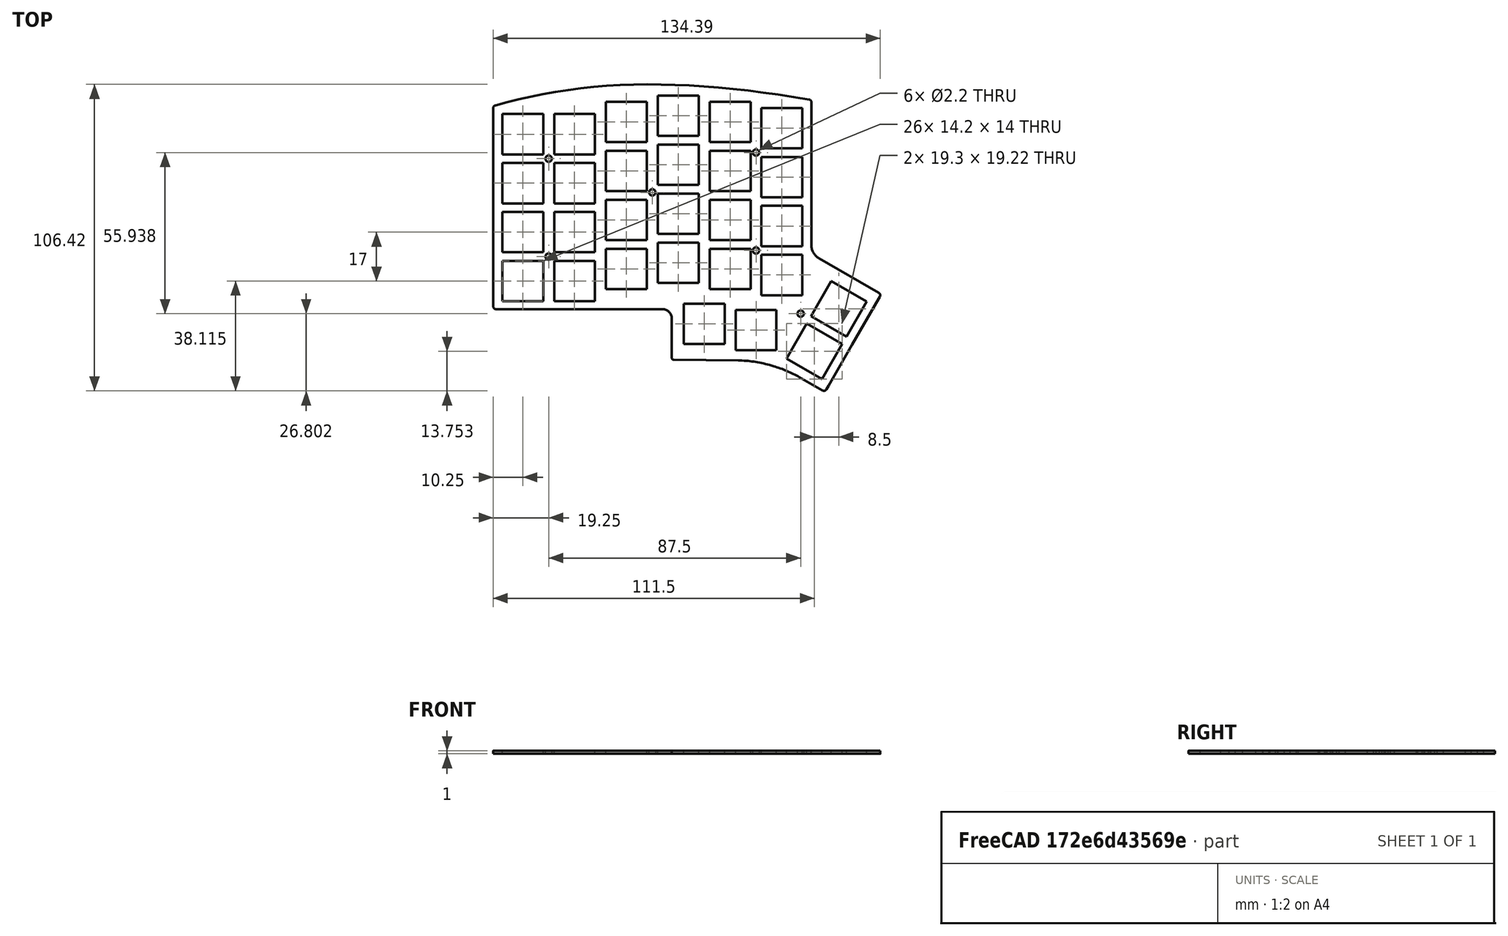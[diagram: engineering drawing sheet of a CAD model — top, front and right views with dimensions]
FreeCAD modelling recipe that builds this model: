
FCSTD DOCUMENT  (FreeCAD 0.19R)
Label: iris_plate_support_extruded
License: All rights reserved
LicenseURL: http://en.wikipedia.org/wiki/All_rights_reserved
objects: Part::Feature×35, Part::Extrusion×35, App::LinkGroup×1, Part::FeaturePython×1
note: 71 computed .brp shape members not serialized (recipe doc carries the construction recipe); baked Part::Feature solids carry a one-line shape summary decoded from their .brp

FEATURE [Part::Feature] Face
  shape: bbox 2.2 x 2.2 x 2e-07 mm, 1 faces, 0 solids (baked)
FEATURE [Part::Feature] Face001 .. Face005  x5 (patterned run collapsed; names and placements below)
  shape: bbox 2.2 x 2.2 x 2e-07 mm, 1 faces, 0 solids (baked)
FEATURE [Part::Feature] Face006 .. Face021  x16 (patterned run collapsed; names and placements below)
  shape: bbox 14.2 x 14 x 2e-07 mm, 1 faces, 0 solids (baked)
FEATURE [Part::Feature] Face022
  shape: bbox 19.3 x 19.22 x 2e-07 mm, 1 faces, 0 solids (baked)
FEATURE [Part::Feature] Face023 .. Face030  x8 (patterned run collapsed; names and placements below)
  shape: bbox 14.2 x 14 x 2e-07 mm, 1 faces, 0 solids (baked)
FEATURE [Part::Feature] Face031
  shape: bbox 19.3 x 19.22 x 2e-07 mm, 1 faces, 0 solids (baked)
FEATURE [Part::Feature] Face032
  shape: bbox 14.2 x 14 x 2e-07 mm, 1 faces, 0 solids (baked)
FEATURE [Part::Feature] Face033
  shape: bbox 14.2 x 14 x 2e-07 mm, 1 faces, 0 solids (baked)
FEATURE [Part::Feature] Face034
  shape: bbox 134.4 x 106.7 x 2e-07 mm, 1 faces, 0 solids (baked)
FEATURE [Part::Extrusion] Extrude
  Base = -> Face034
  Dir = (0,0,1)
  DirMode = 0
  FaceMakerClass = Part::FaceMakerBullseye
  LengthFwd = 1
  LengthRev = 0
  Solid = true
  Symmetric = false
FEATURE [Part::Extrusion] Extrude001
  Base = -> Face033
  Dir = (0,0,1)
  DirMode = 0
  FaceMakerClass = Part::FaceMakerBullseye
  LengthFwd = 1
  LengthRev = 0
  Solid = true
  Symmetric = false
FEATURE [Part::Extrusion] Extrude002
  Base = -> Face032
  Dir = (0,0,1)
  DirMode = 0
  FaceMakerClass = Part::FaceMakerBullseye
  LengthFwd = 1
  LengthRev = 0
  Solid = true
  Symmetric = false
FEATURE [Part::Extrusion] Extrude003
  Base = -> Face031
  Dir = (0,0,1)
  DirMode = 0
  FaceMakerClass = Part::FaceMakerBullseye
  LengthFwd = 1
  LengthRev = 0
  Solid = true
  Symmetric = false
FEATURE [Part::Extrusion] Extrude004
  Base = -> Face030
  Dir = (0,0,1)
  DirMode = 0
  FaceMakerClass = Part::FaceMakerBullseye
  LengthFwd = 1
  LengthRev = 0
  Solid = true
  Symmetric = false
FEATURE [Part::Extrusion] Extrude005
  Base = -> Face029
  Dir = (0,0,1)
  DirMode = 0
  FaceMakerClass = Part::FaceMakerBullseye
  LengthFwd = 1
  LengthRev = 0
  Solid = true
  Symmetric = false
FEATURE [Part::Extrusion] Extrude006
  Base = -> Face028
  Dir = (0,0,1)
  DirMode = 0
  FaceMakerClass = Part::FaceMakerBullseye
  LengthFwd = 1
  LengthRev = 0
  Solid = true
  Symmetric = false
FEATURE [Part::Extrusion] Extrude007
  Base = -> Face027
  Dir = (0,0,1)
  DirMode = 0
  FaceMakerClass = Part::FaceMakerBullseye
  LengthFwd = 1
  LengthRev = 0
  Solid = true
  Symmetric = false
FEATURE [Part::Extrusion] Extrude008
  Base = -> Face026
  Dir = (0,0,1)
  DirMode = 0
  FaceMakerClass = Part::FaceMakerBullseye
  LengthFwd = 1
  LengthRev = 0
  Solid = true
  Symmetric = false
FEATURE [Part::Extrusion] Extrude009
  Base = -> Face025
  Dir = (0,0,1)
  DirMode = 0
  FaceMakerClass = Part::FaceMakerBullseye
  LengthFwd = 1
  LengthRev = 0
  Solid = true
  Symmetric = false
FEATURE [Part::Extrusion] Extrude010
  Base = -> Face024
  Dir = (0,0,1)
  DirMode = 0
  FaceMakerClass = Part::FaceMakerBullseye
  LengthFwd = 1
  LengthRev = 0
  Solid = true
  Symmetric = false
FEATURE [Part::Extrusion] Extrude011
  Base = -> Face023
  Dir = (0,0,1)
  DirMode = 0
  FaceMakerClass = Part::FaceMakerBullseye
  LengthFwd = 1
  LengthRev = 0
  Solid = true
  Symmetric = false
FEATURE [Part::Extrusion] Extrude012
  Base = -> Face022
  Dir = (0,0,1)
  DirMode = 0
  FaceMakerClass = Part::FaceMakerBullseye
  LengthFwd = 1
  LengthRev = 0
  Solid = true
  Symmetric = false
FEATURE [Part::Extrusion] Extrude013
  Base = -> Face021
  Dir = (0,0,1)
  DirMode = 0
  FaceMakerClass = Part::FaceMakerBullseye
  LengthFwd = 1
  LengthRev = 0
  Solid = true
  Symmetric = false
FEATURE [Part::Extrusion] Extrude014
  Base = -> Face020
  Dir = (0,0,1)
  DirMode = 0
  FaceMakerClass = Part::FaceMakerBullseye
  LengthFwd = 1
  LengthRev = 0
  Solid = true
  Symmetric = false
FEATURE [Part::Extrusion] Extrude015
  Base = -> Face019
  Dir = (0,0,1)
  DirMode = 0
  FaceMakerClass = Part::FaceMakerBullseye
  LengthFwd = 1
  LengthRev = 0
  Solid = true
  Symmetric = false
FEATURE [Part::Extrusion] Extrude016
  Base = -> Face018
  Dir = (0,0,1)
  DirMode = 0
  FaceMakerClass = Part::FaceMakerBullseye
  LengthFwd = 1
  LengthRev = 0
  Solid = true
  Symmetric = false
FEATURE [Part::Extrusion] Extrude017
  Base = -> Face017
  Dir = (0,0,1)
  DirMode = 0
  FaceMakerClass = Part::FaceMakerBullseye
  LengthFwd = 1
  LengthRev = 0
  Solid = true
  Symmetric = false
FEATURE [Part::Extrusion] Extrude018
  Base = -> Face016
  Dir = (0,0,1)
  DirMode = 0
  FaceMakerClass = Part::FaceMakerBullseye
  LengthFwd = 1
  LengthRev = 0
  Solid = true
  Symmetric = false
FEATURE [Part::Extrusion] Extrude019
  Base = -> Face015
  Dir = (0,0,1)
  DirMode = 0
  FaceMakerClass = Part::FaceMakerBullseye
  LengthFwd = 1
  LengthRev = 0
  Solid = true
  Symmetric = false
FEATURE [Part::Extrusion] Extrude020
  Base = -> Face014
  Dir = (0,0,1)
  DirMode = 0
  FaceMakerClass = Part::FaceMakerBullseye
  LengthFwd = 1
  LengthRev = 0
  Solid = true
  Symmetric = false
FEATURE [Part::Extrusion] Extrude021
  Base = -> Face013
  Dir = (0,0,1)
  DirMode = 0
  FaceMakerClass = Part::FaceMakerBullseye
  LengthFwd = 1
  LengthRev = 0
  Solid = true
  Symmetric = false
FEATURE [Part::Extrusion] Extrude022
  Base = -> Face012
  Dir = (0,0,1)
  DirMode = 0
  FaceMakerClass = Part::FaceMakerBullseye
  LengthFwd = 1
  LengthRev = 0
  Solid = true
  Symmetric = false
FEATURE [Part::Extrusion] Extrude023
  Base = -> Face011
  Dir = (0,0,1)
  DirMode = 0
  FaceMakerClass = Part::FaceMakerBullseye
  LengthFwd = 1
  LengthRev = 0
  Solid = true
  Symmetric = false
FEATURE [Part::Extrusion] Extrude024
  Base = -> Face010
  Dir = (0,0,1)
  DirMode = 0
  FaceMakerClass = Part::FaceMakerBullseye
  LengthFwd = 1
  LengthRev = 0
  Solid = true
  Symmetric = false
FEATURE [Part::Extrusion] Extrude025
  Base = -> Face009
  Dir = (0,0,1)
  DirMode = 0
  FaceMakerClass = Part::FaceMakerBullseye
  LengthFwd = 1
  LengthRev = 0
  Solid = true
  Symmetric = false
FEATURE [Part::Extrusion] Extrude026
  Base = -> Face008
  Dir = (0,0,1)
  DirMode = 0
  FaceMakerClass = Part::FaceMakerBullseye
  LengthFwd = 1
  LengthRev = 0
  Solid = true
  Symmetric = false
FEATURE [Part::Extrusion] Extrude027
  Base = -> Face007
  Dir = (0,0,1)
  DirMode = 0
  FaceMakerClass = Part::FaceMakerBullseye
  LengthFwd = 1
  LengthRev = 0
  Solid = true
  Symmetric = false
FEATURE [Part::Extrusion] Extrude028
  Base = -> Face006
  Dir = (0,0,1)
  DirMode = 0
  FaceMakerClass = Part::FaceMakerBullseye
  LengthFwd = 1
  LengthRev = 0
  Solid = true
  Symmetric = false
FEATURE [Part::Extrusion] Extrude029
  Base = -> Face005
  Dir = (0,0,1)
  DirMode = 0
  FaceMakerClass = Part::FaceMakerBullseye
  LengthFwd = 1
  LengthRev = 0
  Solid = true
  Symmetric = false
FEATURE [Part::Extrusion] Extrude030
  Base = -> Face004
  Dir = (0,0,1)
  DirMode = 0
  FaceMakerClass = Part::FaceMakerBullseye
  LengthFwd = 1
  LengthRev = 0
  Solid = true
  Symmetric = false
FEATURE [Part::Extrusion] Extrude031
  Base = -> Face003
  Dir = (0,0,1)
  DirMode = 0
  FaceMakerClass = Part::FaceMakerBullseye
  LengthFwd = 1
  LengthRev = 0
  Solid = true
  Symmetric = false
FEATURE [Part::Extrusion] Extrude032
  Base = -> Face002
  Dir = (0,0,1)
  DirMode = 0
  FaceMakerClass = Part::FaceMakerBullseye
  LengthFwd = 1
  LengthRev = 0
  Solid = true
  Symmetric = false
FEATURE [Part::Extrusion] Extrude033
  Base = -> Face001
  Dir = (0,0,1)
  DirMode = 0
  FaceMakerClass = Part::FaceMakerBullseye
  LengthFwd = 1
  LengthRev = 0
  Solid = true
  Symmetric = false
FEATURE [Part::Extrusion] Extrude034
  Base = -> Face
  Dir = (0,0,1)
  DirMode = 0
  FaceMakerClass = Part::FaceMakerBullseye
  LengthFwd = 1
  LengthRev = 0
  Solid = true
  Symmetric = false
FEATURE [App::LinkGroup] LinkGroup
  ElementList = -> [Extrude001,Extrude002,Extrude003,Extrude004,Extrude005,Extrude006,Extrude007,Extrude008,Extrude009,Extrude010,Extrude011,Extrude012,Extrude013,Extrude014,Extrude015,Extrude016,Extrude017,Extrude018,Extrude019,Extrude020,Extrude021,Extrude022,Extrude023,Extrude024,Extrude025,Extrude026,Extrude027,Extrude028,Extrude029,Extrude030,Extrude031,Extrude032,Extrude033,Extrude034]
  LinkMode = 0
FEATURE [Part::FeaturePython] Cutout  # WARN: FeaturePython — macro-defined, semantics opaque (R4)
  Base = -> Extrude
  Tolerance = 0
  Tool = -> LinkGroup
